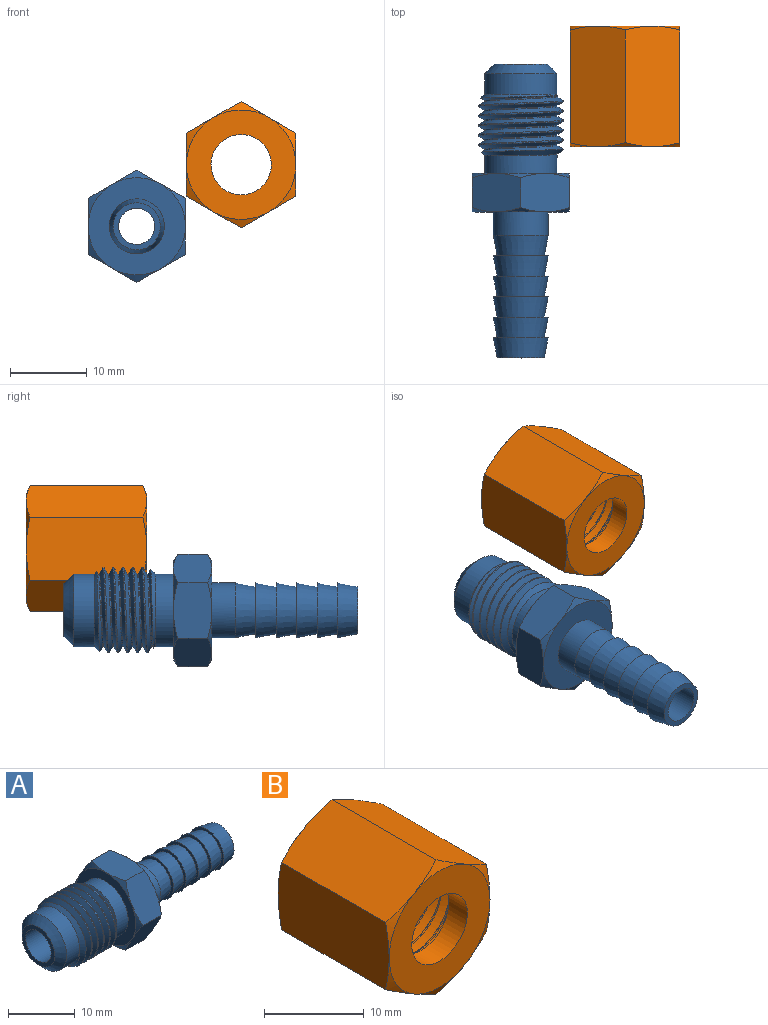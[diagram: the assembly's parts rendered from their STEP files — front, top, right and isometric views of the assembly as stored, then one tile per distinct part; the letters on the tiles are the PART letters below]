
ASSEMBLY  parts=2 mates=1
PART A: 50 faces, bbox 39x15.3x15.3 mm
  f0: cylinder r=5.56mm len=11.11mm, axis (-1,0,0), area 29.4mm2, adj f1,f2,f10,f11
  f1: bspline ~12.83x11.11mm, area 172.3mm2, adj f0,f3,f4,f5,f6,f7,f8,f9
  f2: bspline ~12.83x11.11mm, area 172.3mm2, adj f0,f3,f4,f5,f6,f7,f8,f9
  f3: cylinder r=4.73mm len=9.46mm, axis (1,0,0), area 72.9mm2, adj f1,f2,f4,f10,f14
  f4: cylinder r=4.73mm len=9.46mm, axis (1,0,0), area 4.7mm2, adj f1,f2,f3,f5
  f5: cylinder r=4.73mm len=9.46mm, axis (1,0,0), area 4.7mm2, adj f1,f2,f4,f6
  f6: cylinder r=4.73mm len=9.46mm, axis (1,0,0), area 4.7mm2, adj f1,f2,f5,f7
  f7: cylinder r=4.73mm len=9.46mm, axis (1,0,0), area 4.7mm2, adj f1,f2,f6,f8
  f8: cylinder r=4.73mm len=9.46mm, axis (1,0,0), area 4.7mm2, adj f1,f2,f7,f9
  f9: cylinder r=4.73mm len=9.46mm, axis (1,0,0), area 83.3mm2, adj f1,f2,f8,f11,f12
  f10: cone r=6.42mm half-angle=45deg, axis (-1,0,0), area 18.5mm2, adj f0,f1,f2,f3
  f11: cone r=4.73mm half-angle=45deg, axis (1,0,0), area 18.5mm2, adj f0,f1,f2,f9
  f12: cone r=3.46mm half-angle=45deg, axis (1,0,0), area 46.2mm2, adj f9,f13
  f13: plane 6.92x6.92mm, normal (-1,0,0), area 14.7mm2, adj f12,f47
  f14: plane 12.7x12.7mm, normal (-1,0,0), area 56.3mm2, adj f3,f27,f28,f29,f30,f31,f32
  f15: cone r=3.58mm half-angle=10.8deg, axis (-1,0,0), area 56.8mm2, adj f16,f24
  f16: plane 7.16x7.16mm, normal (-1,0,0), area 10.6mm2, adj f15,f22
  f17: plane 6.15x6.15mm, normal (1,0,0), area 12.1mm2, adj f18,f49
  f18: cone r=3.58mm half-angle=10.8deg, axis (-1,0,0), area 56.8mm2, adj f17,f19
  f19: plane 7.16x7.16mm, normal (-1,0,0), area 10.6mm2, adj f18,f20
  f20: cone r=3.58mm half-angle=10.8deg, axis (-1,0,0), area 56.8mm2, adj f19,f21
  f21: plane 7.16x7.16mm, normal (-1,0,0), area 10.6mm2, adj f20,f22
  f22: cone r=3.58mm half-angle=10.8deg, axis (-1,0,0), area 56.8mm2, adj f16,f21
  f23: cone r=3.58mm half-angle=10.8deg, axis (-1,0,0), area 56.8mm2, adj f24,f26
  f24: plane 7.16x7.16mm, normal (-1,0,0), area 10.6mm2, adj f15,f23
  f25: cone r=3.58mm half-angle=10.8deg, axis (-1,0,0), area 56.8mm2, adj f26,f46
  f26: plane 7.16x7.16mm, normal (-1,0,0), area 10.6mm2, adj f23,f25
  f27: cone r=6.35mm half-angle=60deg, axis (1,0,0), area 4mm2, adj f14,f33,f34
  f28: cone r=6.35mm half-angle=60deg, axis (1,0,0), area 4mm2, adj f14,f34,f35
  f29: cone r=6.35mm half-angle=60deg, axis (1,0,0), area 4mm2, adj f14,f35,f36
  f30: cone r=6.35mm half-angle=60deg, axis (1,0,0), area 4mm2, adj f14,f36,f37
  f31: cone r=6.35mm half-angle=60deg, axis (1,0,0), area 4mm2, adj f14,f33,f38
  f32: cone r=6.35mm half-angle=60deg, axis (1,0,0), area 4mm2, adj f14,f37,f38
  f33: plane 6.95x5.64mm, normal (0,0.87,-0.5), area 34mm2, adj f27,f31,f34,f38,f39,f40
  f34: plane 7.94x5.64mm, normal (0,0,-1), area 34mm2, adj f27,f28,f33,f35,f40,f41
  f35: plane 6.95x5.64mm, normal (0,-0.87,-0.5), area 34mm2, adj f28,f29,f34,f36,f41,f42
  f36: plane 6.95x5.64mm, normal (0,-0.87,0.5), area 34mm2, adj f29,f30,f35,f37,f42,f43
  f37: plane 7.94x5.64mm, normal (0,0,1), area 34mm2, adj f30,f32,f36,f38,f43,f44
  f38: plane 6.95x5.64mm, normal (0,0.87,0.5), area 34mm2, adj f31,f32,f33,f37,f39,f44
  f39: cone r=6.35mm half-angle=60deg, axis (-1,0,0), area 4mm2, adj f33,f38,f45
  f40: cone r=6.35mm half-angle=60deg, axis (-1,0,0), area 4mm2, adj f33,f34,f45
  f41: cone r=6.35mm half-angle=60deg, axis (-1,0,0), area 4mm2, adj f34,f35,f45
  f42: cone r=6.35mm half-angle=60deg, axis (-1,0,0), area 4mm2, adj f35,f36,f45
  f43: cone r=6.35mm half-angle=60deg, axis (-1,0,0), area 4mm2, adj f36,f37,f45
  f44: cone r=6.35mm half-angle=60deg, axis (-1,0,0), area 4mm2, adj f37,f38,f45
  f45: plane 12.7x12.7mm, normal (1,0,0), area 86.4mm2, adj f39,f40,f41,f42,f43,f44,f46
  f46: cylinder r=3.58mm len=7.16mm, axis (1,0,0), area 68.6mm2, adj f25,f45
  f47: cylinder r=2.7mm len=17.27mm, axis (-1,0,0), area 292.9mm2, adj f13,f48
  f48: plane 5.4x5.4mm, normal (-1,0,0), area 5.4mm2, adj f47,f49
  f49: cylinder r=2.36mm len=21.08mm, axis (1,0,0), area 312.9mm2, adj f17,f48
PART B: 26 faces, bbox 17.1x17x17.1 mm
  f0: plane 14.79x14.79mm, normal (0,1,0), area 76.9mm2, adj f2,f3,f4,f5,f18,f19,f20,f21
  f1: plane 14.29x14.29mm, normal (0,-1,0), area 111.6mm2, adj f6,f7,f8,f9,f10,f11,f25
  f2: cylinder r=5.56mm len=13.12mm, axis (0,-1,0), area 57.1mm2, adj f0,f4,f5,f24
  f3: cylinder r=4.73mm len=13.12mm, axis (0,-1,0), area 48.6mm2, adj f0,f4,f5,f24
  f4: bspline ~14.29x11.11mm, area 318.1mm2, adj f0,f2,f3,f24
  f5: bspline ~14.29x11.11mm, area 318.1mm2, adj f0,f2,f3,f24
  f6: cone r=8.25mm half-angle=65deg, axis (0,1,0), area 4.8mm2, adj f1,f13,f14
  f7: cone r=8.25mm half-angle=65deg, axis (0,1,0), area 4.8mm2, adj f1,f12,f13
  f8: cone r=8.25mm half-angle=65deg, axis (0,1,0), area 4.8mm2, adj f1,f12,f17
  f9: cone r=8.25mm half-angle=65deg, axis (0,1,0), area 4.8mm2, adj f1,f16,f17
  f10: cone r=8.25mm half-angle=65deg, axis (0,1,0), area 4.8mm2, adj f1,f15,f16
  f11: cone r=8.25mm half-angle=65deg, axis (0,1,0), area 4.8mm2, adj f1,f14,f15
  f12: plane 16.4x8.9mm, normal (1,0,0), area 127mm2, adj f7,f8,f13,f17,f18,f19
  f13: plane 16.4x7.79mm, normal (0.5,0,0.87), area 127mm2, adj f6,f7,f12,f14,f18,f20
  f14: plane 16.4x7.79mm, normal (-0.5,0,0.87), area 127mm2, adj f6,f11,f13,f15,f20,f21
  f15: plane 16.4x8.9mm, normal (-1,0,0), area 127mm2, adj f10,f11,f14,f16,f21,f22
  f16: plane 16.4x7.79mm, normal (-0.5,0,-0.87), area 127mm2, adj f9,f10,f15,f17,f22,f23
  f17: plane 16.4x7.79mm, normal (0.5,0,-0.87), area 127mm2, adj f8,f9,f12,f16,f19,f23
  f18: cone r=7.14mm half-angle=65deg, axis (0,-1,0), area 4.8mm2, adj f0,f12,f13
  f19: cone r=7.14mm half-angle=65deg, axis (0,-1,0), area 4.8mm2, adj f0,f12,f17
  f20: cone r=7.14mm half-angle=65deg, axis (0,-1,0), area 4.8mm2, adj f0,f13,f14
  f21: cone r=7.14mm half-angle=65deg, axis (0,-1,0), area 4.8mm2, adj f0,f14,f15
  f22: cone r=7.14mm half-angle=65deg, axis (0,-1,0), area 4.8mm2, adj f0,f15,f16
  f23: cone r=7.14mm half-angle=65deg, axis (0,-1,0), area 4.8mm2, adj f0,f16,f17
  f24: plane 10.83x10.81mm, normal (0,1,0), area 34.7mm2, adj f2,f3,f4,f5,f25
  f25: cylinder r=3.94mm len=7.87mm, axis (0,-1,0), area 64.9mm2, adj f1,f24
PLACE A rot(axis=(0.58,-0.58,-0.58),120deg) t=(-13.62,-8.37,-8.05)mm
PLACE B at identity
MATE parallel A.f10 <-> B.f0  axis (0,1,0) through (-13.62,10.81,-8.05)mm
